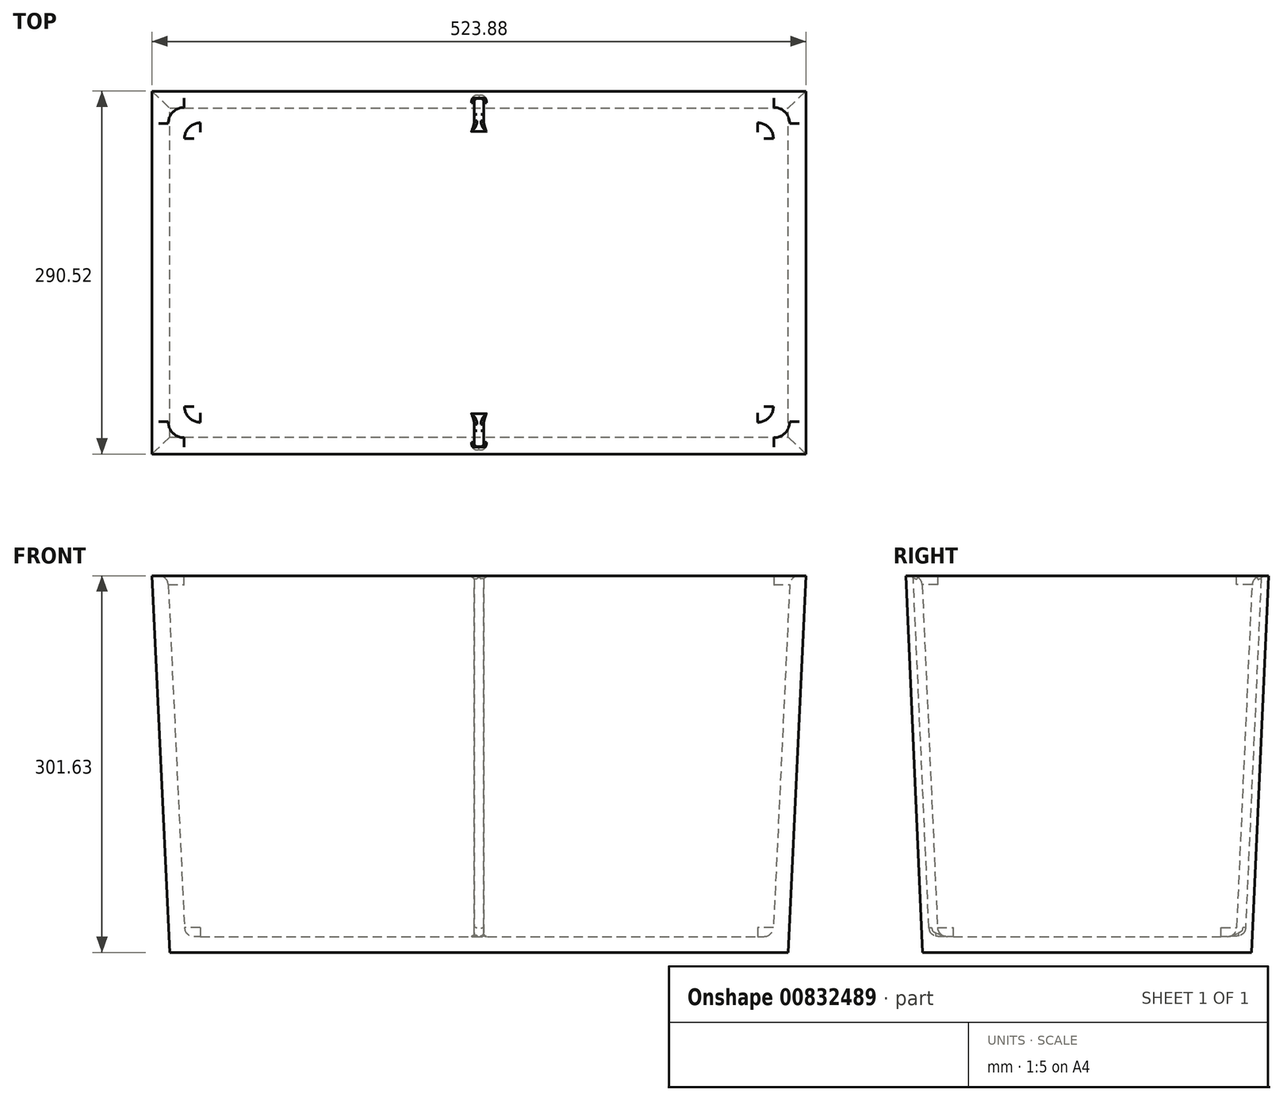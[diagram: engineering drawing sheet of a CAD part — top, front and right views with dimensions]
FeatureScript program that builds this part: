
annotation { "Feature Type Name" : "Feature", "Feature Type Description" : "" }
export const myFeature = defineFeature(function(context is Context, id is Id, definition is map)
    precondition{}
    {
        {
            var Q0;
            Q0=qCreatedBy(makeId("Front.planeOp"),FACE);
            var sketch = newSketch(context, id + "F0", { "sketchPlane" : qUnion([Q0])});
            skLineSegment(sketch, "E0", {"start": v(-261.94, 301.63) * mm, "end": v(-247.65, 0) * mm});
            skLineSegment(sketch, "E1", {"start": v(-247.65, 0) * mm, "end": v(247.65, 0) * mm});
            skLineSegment(sketch, "E2", {"start": v(247.65, 0) * mm, "end": v(261.94, 301.63) * mm});
            skLineSegment(sketch, "E3", {"start": v(261.94, 301.63) * mm, "end": v(-261.94, 301.62) * mm});
            skSolve(sketch);
        }
        {
            var Q0;
            Q0=qSketchRegion(id+"F0",true);
            extrude(context, id + "F1", {"entities" : qUnion([Q0]), "endBound" : BoundingType.SYMMETRIC, "depth" : 304.8 * mm, "offsetDistance" : 25.4 * mm});
        }
        {
            var Q0;
            Q0=qCreatedBy(makeId("Right.planeOp"),FACE);
            var sketch = newSketch(context, id + "F2", { "sketchPlane" : qUnion([Q0])});
            skLineSegment(sketch, "E4", {"start": v(145.26, 301.63) * mm, "end": v(131.76, 0) * mm});
            skLineSegment(sketch, "E5", {"start": v(131.76, 0) * mm, "end": v(-131.76, 0) * mm});
            skLineSegment(sketch, "E6", {"start": v(-131.76, 0) * mm, "end": v(-145.26, 301.63) * mm});
            skLineSegment(sketch, "E7", {"start": v(-145.26, 301.63) * mm, "end": v(145.26, 301.63) * mm});
            skLineSegment(sketch, "E8.bottom", {"start": v(209.57, 350.87) * mm, "end": v(-251.45, 350.87) * mm});
            skLineSegment(sketch, "E8.top", {"start": v(209.57, -64.68) * mm, "end": v(-251.45, -64.68) * mm});
            skLineSegment(sketch, "E8.left", {"start": v(209.57, 350.87) * mm, "end": v(209.57, -64.68) * mm});
            skLineSegment(sketch, "E8.right", {"start": v(-251.45, 350.87) * mm, "end": v(-251.45, -64.68) * mm});
            skSolve(sketch);
        }
        {
            var Q0;
            Q0=makeQuery(id+"F2.imprint","IMPRINT",FACE,{"disambiguationData":[TD([[makeQuery(id+"F2.imprint","IMPRINT",EDGE,{"derivedFrom":sQuery(id+"F2.wireOp",EDGE,"E4")}),1.0]])]});
            extrude(context, id + "F3", {"entities" : qUnion([Q0]), "operationType" : NewBodyOperationType.REMOVE, "endBound" : BoundingType.SYMMETRIC, "oppositeDirection" : true, "depth" : 635 * mm, "offsetDistance" : 25.4 * mm});
        }
        {
            var Q0;
            Q0=makeQuery(id+"F1.opExtrude","SWEPT_FACE",FACE,{"disambiguationData":[OSD([sQuery(id+"F0.wireOp",EDGE,"E3")])]});
            shell(context, id + "F4", {"entities" : qUnion([Q0]), "thickness" : 12.7 * mm});
        }
        {
            var Q0;
            Q0=makeQuery(id+"F4.opShell","OFFSET_EDGE",EDGE,{"disambiguationData":[OSD([sQuery(id+"F0.wireOp",EDGE,"E2"),sQuery(id+"F2.wireOp",EDGE,"E4")])]});
            var Q1;
            Q1=makeQuery(id+"F4.opShell","OFFSET_EDGE",EDGE,{"disambiguationData":[OSD([sQuery(id+"F0.wireOp",EDGE,"E2"),sQuery(id+"F2.wireOp",EDGE,"E6")])]});
            var Q2;
            Q2=makeQuery(id+"F4.opShell","OFFSET_EDGE",EDGE,{"disambiguationData":[OSD([sQuery(id+"F0.wireOp",EDGE,"E0"),sQuery(id+"F2.wireOp",EDGE,"E4")])]});
            var Q3;
            Q3=makeQuery(id+"F4.opShell","OFFSET_EDGE",EDGE,{"disambiguationData":[OSD([sQuery(id+"F0.wireOp",EDGE,"E0"),sQuery(id+"F2.wireOp",EDGE,"E6")])]});
            fillet(context, id + "F5", {"entities" : qUnion([Q0, Q1, Q2, Q3]), "radius" : 12.7 * mm, "tangentPropagation" : true, "allowEdgeOverflow" : false});
        }
        {
            var Q0;
            Q0=makeQuery(id+"F4.opShell","OFFSET_EDGE",EDGE,{"disambiguationData":[OSD([sQuery(id+"F2.wireOp",EDGE,"E4"),sQuery(id+"F2.wireOp",EDGE,"E5")])]});
            fillet(context, id + "F6", {"entities" : qUnion([Q0]), "radius" : 7.62 * mm, "tangentPropagation" : true, "allowEdgeOverflow" : false});
        }
        {
            var Q0;
            Q0=qCreatedBy(makeId("Right.planeOp"),FACE);
            var sketch = newSketch(context, id + "F7", { "sketchPlane" : qUnion([Q0])});
            skLineSegment(sketch, "E9.0", {"start": v(139.4, 301.63) * mm, "end": v(126.8, 19.67) * mm});
            skLineSegment(sketch, "E10.0", {"start": v(-126.8, 19.67) * mm, "end": v(-139.4, 301.63) * mm});
            skFitSpline(sketch, "E11", {"points": [v(126.8, 19.67) * mm, v(123.37, 14.05) * mm, v(107.26, 12.7) * mm], "startDerivative": vector(-2.09, -26.96) * mm, "endDerivative": vector(-49.8, -0.04) * mm});
            skFitSpline(sketch, "E12.MirrorCS", {"points": [v(-126.8, 19.67) * mm, v(-123.37, 14.05) * mm, v(-107.26, 12.7) * mm], "startDerivative": vector(2.09, -26.96) * mm, "endDerivative": vector(49.8, -0.04) * mm});
            skLineSegment(sketch, "E13", {"start": v(107.26, 12.7) * mm, "end": v(-107.26, 12.7) * mm});
            skLineSegment(sketch, "E14", {"start": v(-139.4, 301.63) * mm, "end": v(139.4, 301.63) * mm});
            skSolve(sketch);
        }
        {
            var Q0;
            Q0=qSketchRegion(id+"F7",true);
            extrude(context, id + "F8", {"entities" : qUnion([Q0]), "operationType" : NewBodyOperationType.REMOVE, "endBound" : BoundingType.SYMMETRIC, "oppositeDirection" : true, "depth" : 7.62 * mm, "offsetDistance" : 25.4 * mm});
        }
        {
            var Q0;
            Q0=makeQuery(id+"F8.boolean.opBoolean","COPY",EDGE,{"derivedFrom":makeQuery(id+"F8.opExtrude","CAP_EDGE",EDGE,{"disambiguationData":[OSD([sQuery(id+"F7.wireOp",EDGE,"E9.0")])],"isStart":true})});
            var Q1;
            Q1=makeQuery(id+"F8.boolean.opBoolean","COPY",EDGE,{"derivedFrom":makeQuery(id+"F8.opExtrude","CAP_EDGE",EDGE,{"disambiguationData":[OSD([sQuery(id+"F7.wireOp",EDGE,"E9.0")])],"isStart":false})});
            var Q2;
            Q2=makeQuery(id+"F8.boolean.opBoolean","INTERSECT",EDGE,{"derivedFrom":[makeQuery(id+"F4.opShell","OFFSET_FACE",FACE,{"disambiguationData":[OSD([sQuery(id+"F2.wireOp",EDGE,"E4")])]}),makeQuery(id+"F8.opExtrude","CAP_FACE",FACE,{"disambiguationData":[OSD([sQuery(id+"F7.wireOp",EDGE,"E9.0"),sQuery(id+"F7.wireOp",EDGE,"E10.0"),sQuery(id+"F7.wireOp",EDGE,"E11"),sQuery(id+"F7.wireOp",EDGE,"E12.MirrorCS"),sQuery(id+"F7.wireOp",EDGE,"E13"),sQuery(id+"F7.wireOp",EDGE,"E14")])],"isStart":false})]});
            var Q3;
            Q3=makeQuery(id+"F8.boolean.opBoolean","INTERSECT",EDGE,{"derivedFrom":[makeQuery(id+"F4.opShell","OFFSET_FACE",FACE,{"disambiguationData":[OSD([sQuery(id+"F2.wireOp",EDGE,"E4")])]}),makeQuery(id+"F8.opExtrude","CAP_FACE",FACE,{"disambiguationData":[OSD([sQuery(id+"F7.wireOp",EDGE,"E9.0"),sQuery(id+"F7.wireOp",EDGE,"E10.0"),sQuery(id+"F7.wireOp",EDGE,"E11"),sQuery(id+"F7.wireOp",EDGE,"E12.MirrorCS"),sQuery(id+"F7.wireOp",EDGE,"E13"),sQuery(id+"F7.wireOp",EDGE,"E14")])],"isStart":true})]});
            var Q4;
            Q4=makeQuery(id+"F8.boolean.opBoolean","COPY",EDGE,{"derivedFrom":makeQuery(id+"F8.opExtrude","CAP_EDGE",EDGE,{"disambiguationData":[OSD([sQuery(id+"F7.wireOp",EDGE,"E10.0")])],"isStart":true})});
            var Q5;
            Q5=makeQuery(id+"F8.boolean.opBoolean","INTERSECT",EDGE,{"derivedFrom":[makeQuery(id+"F4.opShell","OFFSET_FACE",FACE,{"disambiguationData":[OSD([sQuery(id+"F2.wireOp",EDGE,"E6")])]}),makeQuery(id+"F8.opExtrude","CAP_FACE",FACE,{"disambiguationData":[OSD([sQuery(id+"F7.wireOp",EDGE,"E9.0"),sQuery(id+"F7.wireOp",EDGE,"E10.0"),sQuery(id+"F7.wireOp",EDGE,"E11"),sQuery(id+"F7.wireOp",EDGE,"E12.MirrorCS"),sQuery(id+"F7.wireOp",EDGE,"E13"),sQuery(id+"F7.wireOp",EDGE,"E14")])],"isStart":true})]});
            var Q6;
            Q6=makeQuery(id+"F8.boolean.opBoolean","INTERSECT",EDGE,{"derivedFrom":[makeQuery(id+"F4.opShell","OFFSET_FACE",FACE,{"disambiguationData":[OSD([sQuery(id+"F2.wireOp",EDGE,"E6")])]}),makeQuery(id+"F8.opExtrude","CAP_FACE",FACE,{"disambiguationData":[OSD([sQuery(id+"F7.wireOp",EDGE,"E9.0"),sQuery(id+"F7.wireOp",EDGE,"E10.0"),sQuery(id+"F7.wireOp",EDGE,"E11"),sQuery(id+"F7.wireOp",EDGE,"E12.MirrorCS"),sQuery(id+"F7.wireOp",EDGE,"E13"),sQuery(id+"F7.wireOp",EDGE,"E14")])],"isStart":false})]});
            var Q7;
            Q7=makeQuery(id+"F8.boolean.opBoolean","COPY",EDGE,{"derivedFrom":makeQuery(id+"F8.opExtrude","CAP_EDGE",EDGE,{"disambiguationData":[OSD([sQuery(id+"F7.wireOp",EDGE,"E10.0")])],"isStart":false})});
            fillet(context, id + "F9", {"entities" : qUnion([Q0, Q1, Q2, Q3, Q4, Q5, Q6, Q7]), "radius" : 2.3 * mm, "tangentPropagation" : true, "allowEdgeOverflow" : false});
        }
        {
            var Q0;
            {var subQ0=sQuery(id+"F7.wireOp",EDGE,"E12.MirrorCS");Q0=makeQuery(id+"F9.opFillet","BLEND_EDGE",EDGE,{"blendedFrom":[makeQuery(id+"F8.boolean.opBoolean","INTERSECT",EDGE,{"derivedFrom":[makeQuery(id+"F6.opFillet","BLEND_FACE",FACE,{"disambiguationData":[OSD([sQuery(id+"F2.wireOp",EDGE,"E5"),sQuery(id+"F2.wireOp",EDGE,"E6")])]}),makeQuery(id+"F8.opExtrude","CAP_FACE",FACE,{"disambiguationData":[OSD([sQuery(id+"F7.wireOp",EDGE,"E9.0"),sQuery(id+"F7.wireOp",EDGE,"E10.0"),sQuery(id+"F7.wireOp",EDGE,"E11"),subQ0,sQuery(id+"F7.wireOp",EDGE,"E13"),sQuery(id+"F7.wireOp",EDGE,"E14")])],"isStart":true})]}),makeQuery(id+"F8.boolean.opBoolean","COPY",FACE,{"derivedFrom":makeQuery(id+"F8.opExtrude","SWEPT_FACE",FACE,{"disambiguationData":[OSD([subQ0])]})})],"blendedInto":[makeQuery(id+"F8.boolean.opBoolean","COPY",FACE,{"derivedFrom":makeQuery(id+"F8.opExtrude","SWEPT_FACE",FACE,{"disambiguationData":[OSD([subQ0])]})})]});}
            var Q1;
            {var subQ0=sQuery(id+"F7.wireOp",EDGE,"E11");Q1=makeQuery(id+"F9.opFillet","BLEND_EDGE",EDGE,{"blendedFrom":[makeQuery(id+"F8.boolean.opBoolean","INTERSECT",EDGE,{"derivedFrom":[makeQuery(id+"F6.opFillet","BLEND_FACE",FACE,{"disambiguationData":[OSD([sQuery(id+"F2.wireOp",EDGE,"E4"),sQuery(id+"F2.wireOp",EDGE,"E5")])]}),makeQuery(id+"F8.opExtrude","CAP_FACE",FACE,{"disambiguationData":[OSD([sQuery(id+"F7.wireOp",EDGE,"E9.0"),sQuery(id+"F7.wireOp",EDGE,"E10.0"),subQ0,sQuery(id+"F7.wireOp",EDGE,"E12.MirrorCS"),sQuery(id+"F7.wireOp",EDGE,"E13"),sQuery(id+"F7.wireOp",EDGE,"E14")])],"isStart":true})]}),makeQuery(id+"F8.boolean.opBoolean","COPY",FACE,{"derivedFrom":makeQuery(id+"F8.opExtrude","SWEPT_FACE",FACE,{"disambiguationData":[OSD([subQ0])]})})],"blendedInto":[makeQuery(id+"F8.boolean.opBoolean","COPY",FACE,{"derivedFrom":makeQuery(id+"F8.opExtrude","SWEPT_FACE",FACE,{"disambiguationData":[OSD([subQ0])]})})]});}
            fillet(context, id + "F10", {"entities" : qUnion([Q0, Q1]), "radius" : 2.3 * mm, "tangentPropagation" : true, "allowEdgeOverflow" : false});
        }
    });
